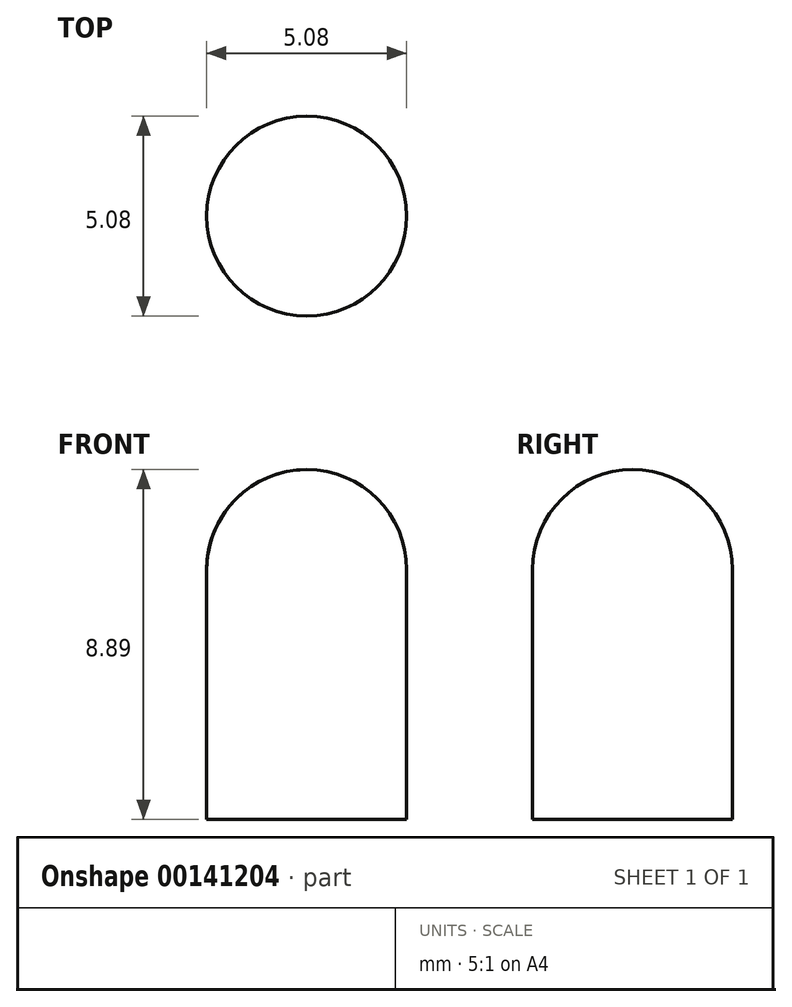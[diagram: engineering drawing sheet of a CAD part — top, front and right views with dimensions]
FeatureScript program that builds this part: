
annotation { "Feature Type Name" : "Feature", "Feature Type Description" : "" }
export const myFeature = defineFeature(function(context is Context, id is Id, definition is map)
    precondition{}
    {
        {
            var Q0;
            Q0=qCreatedBy(makeId("Front.planeOp"),FACE);
            var sketch = newSketch(context, id + "F0", { "sketchPlane" : qUnion([Q0])});
            skLineSegment(sketch, "E0.top", {"start": v(13.66, 5.1) * mm, "end": v(16.2, 5.1) * mm});
            skLineSegment(sketch, "E0.left", {"start": v(13.66, 11.45) * mm, "end": v(13.66, 5.1) * mm});
            skArc(sketch, "E1", {"start": v(16.2, 13.99) * mm, "mid": v(14.4, 13.24) * mm, "end": v(13.66, 11.45) * mm});
            skLineSegment(sketch, "E2", {"start": v(16.2, 13.99) * mm, "end": v(16.2, 5.1) * mm});
            skPoint(sketch, "E3.orphan", {"position": v(18.74, 5.1) * mm});
            skSolve(sketch);
        }
        {
            var Q0;
            Q0=makeQuery(id+"F0.imprint","IMPRINT",FACE,{"disambiguationData":[TD([[makeQuery(id+"F0.imprint","IMPRINT",EDGE,{"derivedFrom":sQuery(id+"F0.wireOp",EDGE,"E0.top")}),1.0]])]});
            var Q1;
            Q1=sQuery(id+"F0.wireOp",EDGE,"E2");
            revolve(context, id + "F1", {"entities" : qUnion([Q0]), "axis" : qUnion([Q1]), "revolveType" : RevolveType.FULL});
        }
    });
